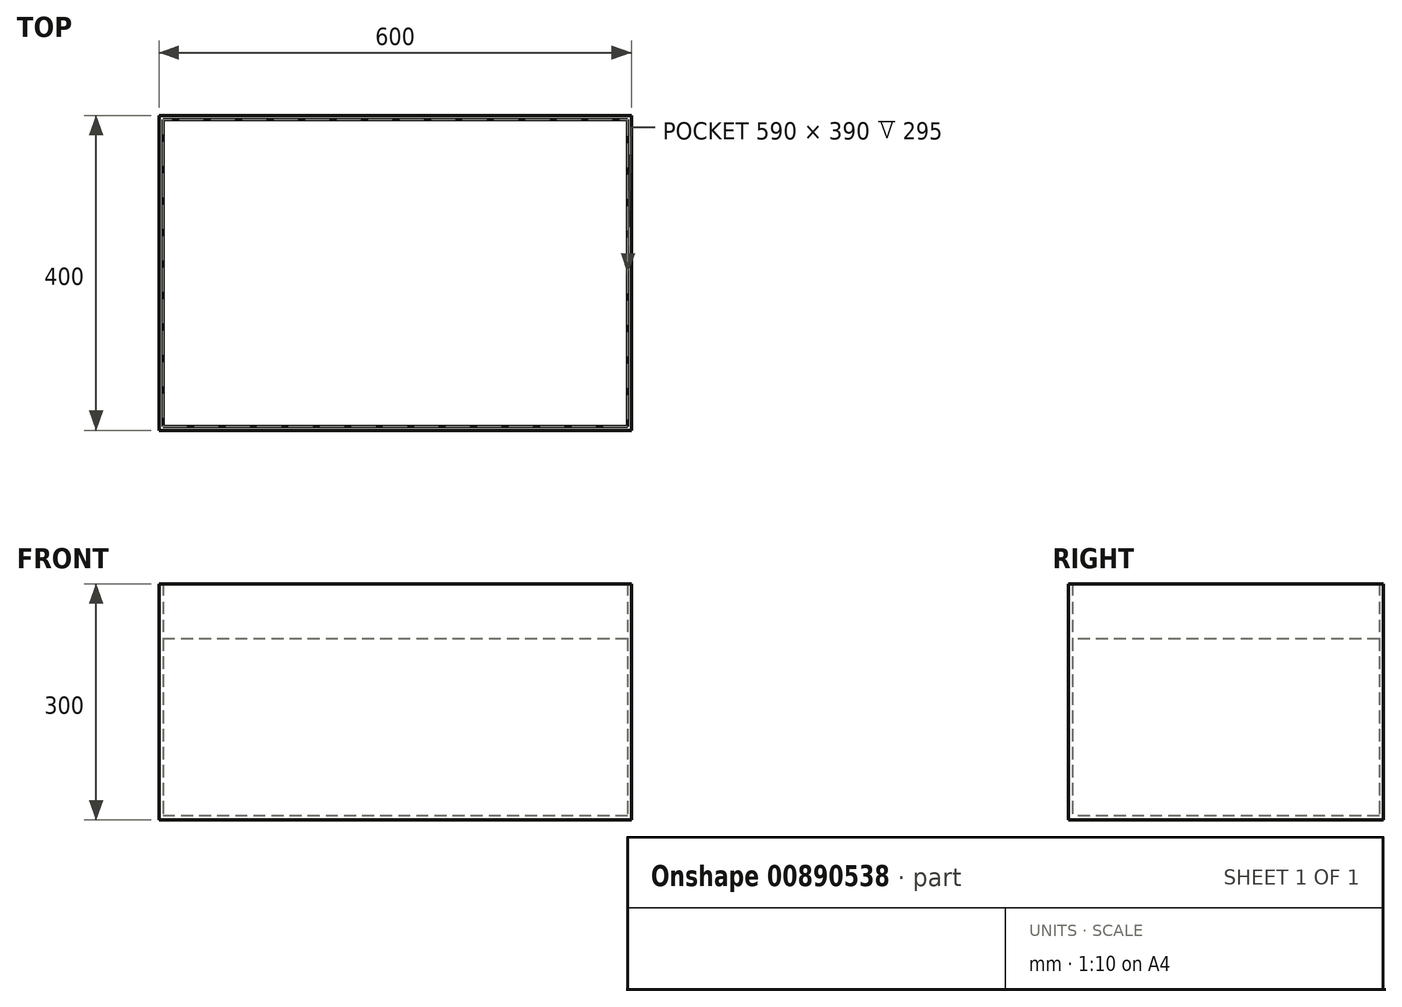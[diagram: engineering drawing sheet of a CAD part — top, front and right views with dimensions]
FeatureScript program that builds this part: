
annotation { "Feature Type Name" : "Feature", "Feature Type Description" : "" }
export const myFeature = defineFeature(function(context is Context, id is Id, definition is map)
    precondition{}
    {
        {
            var Q0;
            Q0=qCreatedBy(makeId("Top.planeOp"),FACE);
            var sketch = newSketch(context, id + "F0", { "sketchPlane" : qUnion([Q0])});
            skLineSegment(sketch, "E0.bottom", {"start": v(300, 200) * mm, "end": v(-300, 200) * mm});
            skLineSegment(sketch, "E0.top", {"start": v(300, -200) * mm, "end": v(-300, -200) * mm});
            skLineSegment(sketch, "E0.left", {"start": v(300, 200) * mm, "end": v(300, -200) * mm});
            skLineSegment(sketch, "E0.right", {"start": v(-300, 200) * mm, "end": v(-300, -200) * mm});
            skPoint(sketch, "E0.middle", {"position": v(0, 0) * mm});
            skSolve(sketch);
        }
        {
            var Q0;
            Q0=makeQuery(id+"F0.imprint","IMPRINT",FACE,{"disambiguationData":[TD([[makeQuery(id+"F0.imprint","IMPRINT",EDGE,{"derivedFrom":sQuery(id+"F0.wireOp",EDGE,"E0.bottom")}),1.0]])]});
            extrude(context, id + "F1", {"entities" : qUnion([Q0]), "depth" : 300 * mm, "offsetDistance" : 25 * mm});
        }
        {
            var Q0;
            Q0=makeQuery(id+"F1.opExtrude","CAP_FACE",FACE,{"disambiguationData":[OSD([sQuery(id+"F0.wireOp",EDGE,"E0.bottom"),sQuery(id+"F0.wireOp",EDGE,"E0.top"),sQuery(id+"F0.wireOp",EDGE,"E0.left"),sQuery(id+"F0.wireOp",EDGE,"E0.right")])],"isStart":false});
            shell(context, id + "F2", {"entities" : qUnion([Q0]), "thickness" : 5 * mm});
        }
        {
            var Q0;
            Q0=makeQuery(id+"F2.opShell","OFFSET_FACE",FACE,{"disambiguationData":[OSD([sQuery(id+"F0.wireOp",EDGE,"E0.bottom"),sQuery(id+"F0.wireOp",EDGE,"E0.top"),sQuery(id+"F0.wireOp",EDGE,"E0.left"),sQuery(id+"F0.wireOp",EDGE,"E0.right")])]});
            var sketch = newSketch(context, id + "F3", { "sketchPlane" : qUnion([Q0])});
            skSolve(sketch);
        }
        {
            var Q0;
            Q0 = qSketchRegion(id + "F3", true);
            var Q1;
            {var subQ0=sQuery(id+"F0.wireOp",EDGE,"E0.bottom");Q1=makeQuery(id+"F3.imprint","IMPRINT",FACE,{"disambiguationData":[TD([[makeQuery(id+"F3.imprint","IMPRINT",EDGE,{"derivedFrom":makeQuery(id+"F2.opShell","OFFSET_EDGE",EDGE,{"disambiguationData":[OSD([subQ0]),TDD([makeQuery(id+"F1.opExtrude","CAP_EDGE",EDGE,{"disambiguationData":[OSD([subQ0])],"isStart":true})])]})}),1.0]])]});}
            extrude(context, id + "F4", {"entities" : qUnion([Q0, Q1]), "depth" : 225 * mm, "offsetDistance" : 25 * mm});
        }
    });
